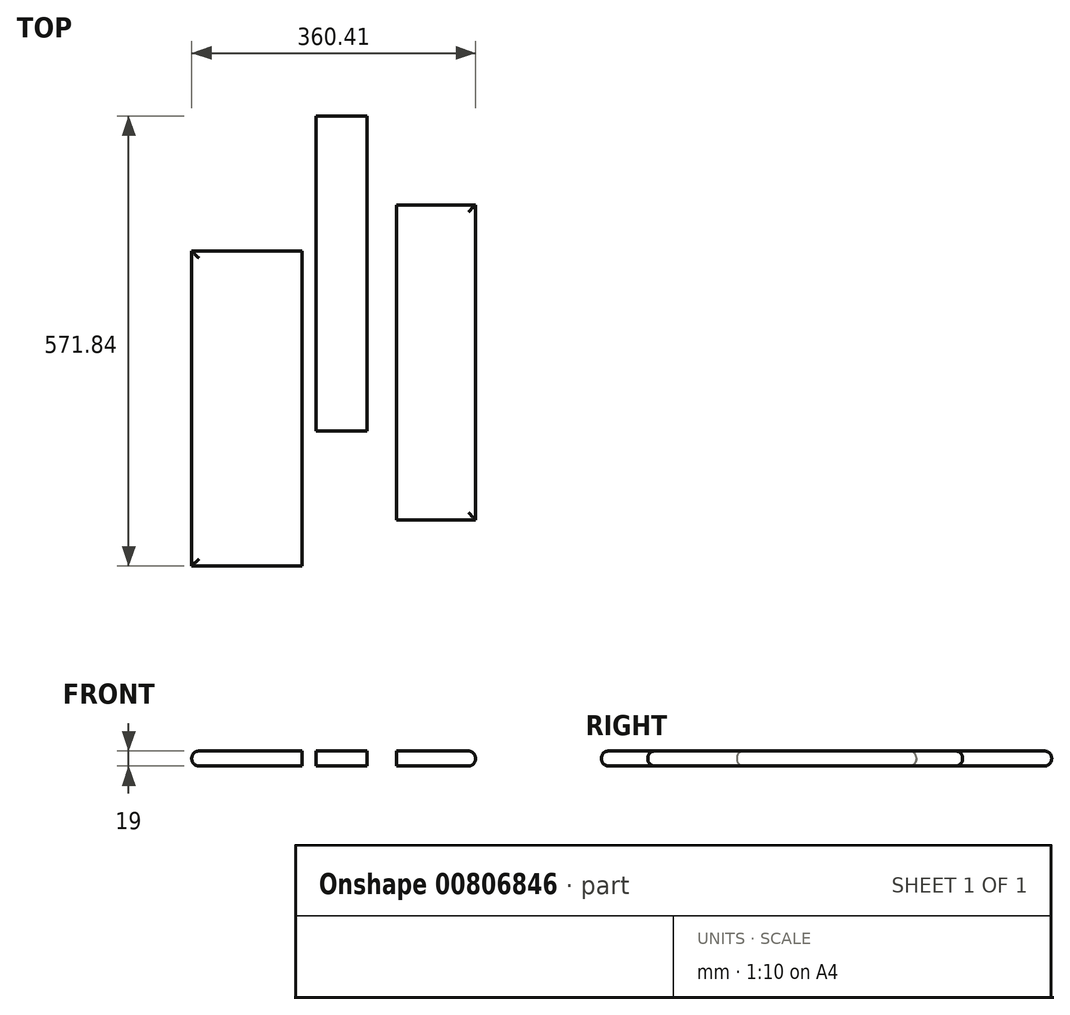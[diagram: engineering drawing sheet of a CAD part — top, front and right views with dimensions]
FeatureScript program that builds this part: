
annotation { "Feature Type Name" : "Feature", "Feature Type Description" : "" }
export const myFeature = defineFeature(function(context is Context, id is Id, definition is map)
    precondition{}
    {
        {
            var Q0;
            Q0=qCreatedBy(makeId("Top.planeOp"),FACE);
            var sketch = newSketch(context, id + "F0", { "sketchPlane" : qUnion([Q0])});
            skLineSegment(sketch, "E0.bottom", {"start": v(-82.9, -190.4) * mm, "end": v(57.1, -190.4) * mm});
            skLineSegment(sketch, "E0.top", {"start": v(-82.9, 209.6) * mm, "end": v(57.1, 209.6) * mm});
            skLineSegment(sketch, "E0.left", {"start": v(-82.9, -190.4) * mm, "end": v(-82.9, 209.6) * mm});
            skLineSegment(sketch, "E0.right", {"start": v(57.1, -190.4) * mm, "end": v(57.1, 209.6) * mm});
            skSolve(sketch);
        }
        {
            var Q0;
            Q0=qCreatedBy(makeId("Top.planeOp"),FACE);
            var sketch = newSketch(context, id + "F1", { "sketchPlane" : qUnion([Q0])});
            skLineSegment(sketch, "E1.bottom", {"start": v(74.78, 381.44) * mm, "end": v(139.78, 381.44) * mm});
            skLineSegment(sketch, "E1.top", {"start": v(74.78, -18.56) * mm, "end": v(139.78, -18.56) * mm});
            skLineSegment(sketch, "E1.left", {"start": v(74.78, 381.44) * mm, "end": v(74.78, -18.56) * mm});
            skLineSegment(sketch, "E1.right", {"start": v(139.78, 381.44) * mm, "end": v(139.78, -18.56) * mm});
            skSolve(sketch);
        }
        {
            var Q0;
            Q0=qCreatedBy(makeId("Top.planeOp"),FACE);
            var sketch = newSketch(context, id + "F2", { "sketchPlane" : qUnion([Q0])});
            skLineSegment(sketch, "E2.bottom", {"start": v(177.5, 268.41) * mm, "end": v(277.5, 268.41) * mm});
            skLineSegment(sketch, "E2.top", {"start": v(177.5, -131.59) * mm, "end": v(277.5, -131.59) * mm});
            skLineSegment(sketch, "E2.left", {"start": v(177.5, 268.41) * mm, "end": v(177.5, -131.59) * mm});
            skLineSegment(sketch, "E2.right", {"start": v(277.5, 268.41) * mm, "end": v(277.5, -131.59) * mm});
            skSolve(sketch);
        }
        {
            var Q0;
            Q0=makeQuery(id+"F0.imprint","IMPRINT",FACE,{"disambiguationData":[TD([[makeQuery(id+"F0.imprint","IMPRINT",EDGE,{"derivedFrom":sQuery(id+"F0.wireOp",EDGE,"E0.bottom")}),1.0]])]});
            extrude(context, id + "F3", {"entities" : qUnion([Q0]), "depth" : 19 * mm, "offsetDistance" : 25 * mm});
        }
        {
            var Q0;
            Q0=makeQuery(id+"F1.imprint","IMPRINT",FACE,{"disambiguationData":[TD([[makeQuery(id+"F1.imprint","IMPRINT",EDGE,{"derivedFrom":sQuery(id+"F1.wireOp",EDGE,"E1.bottom")}),-1.0]])]});
            extrude(context, id + "F4", {"entities" : qUnion([Q0]), "depth" : 19 * mm, "offsetDistance" : 25 * mm});
        }
        {
            var Q0;
            Q0=makeQuery(id+"F2.imprint","IMPRINT",FACE,{"disambiguationData":[TD([[makeQuery(id+"F2.imprint","IMPRINT",EDGE,{"derivedFrom":sQuery(id+"F2.wireOp",EDGE,"E2.bottom")}),-1.0]])]});
            extrude(context, id + "F5", {"entities" : qUnion([Q0]), "depth" : 19 * mm, "offsetDistance" : 25 * mm});
        }
        {
            var Q0;
            Q0=makeQuery(id+"F3.opExtrude","CAP_EDGE",EDGE,{"disambiguationData":[OSD([sQuery(id+"F0.wireOp",EDGE,"E0.bottom")])],"isStart":false});
            var Q1;
            Q1=makeQuery(id+"F3.opExtrude","CAP_EDGE",EDGE,{"disambiguationData":[OSD([sQuery(id+"F0.wireOp",EDGE,"E0.left")])],"isStart":false});
            var Q2;
            Q2=makeQuery(id+"F3.opExtrude","CAP_EDGE",EDGE,{"disambiguationData":[OSD([sQuery(id+"F0.wireOp",EDGE,"E0.top")])],"isStart":false});
            var Q3;
            Q3=makeQuery(id+"F3.opExtrude","CAP_EDGE",EDGE,{"disambiguationData":[OSD([sQuery(id+"F0.wireOp",EDGE,"E0.bottom")])],"isStart":true});
            var Q4;
            Q4=makeQuery(id+"F3.opExtrude","CAP_EDGE",EDGE,{"disambiguationData":[OSD([sQuery(id+"F0.wireOp",EDGE,"E0.left")])],"isStart":true});
            var Q5;
            Q5=makeQuery(id+"F3.opExtrude","CAP_EDGE",EDGE,{"disambiguationData":[OSD([sQuery(id+"F0.wireOp",EDGE,"E0.top")])],"isStart":true});
            fillet(context, id + "F6", {"entities" : qUnion([Q0, Q1, Q2, Q3, Q4, Q5]), "radius" : 9 * mm, "tangentPropagation" : true, "allowEdgeOverflow" : false});
        }
        {
            var Q0;
            Q0=makeQuery(id+"F4.opExtrude","CAP_EDGE",EDGE,{"disambiguationData":[OSD([sQuery(id+"F1.wireOp",EDGE,"E1.bottom")])],"isStart":false});
            var Q1;
            Q1=makeQuery(id+"F4.opExtrude","CAP_EDGE",EDGE,{"disambiguationData":[OSD([sQuery(id+"F1.wireOp",EDGE,"E1.bottom")])],"isStart":true});
            var Q2;
            Q2=makeQuery(id+"F4.opExtrude","CAP_EDGE",EDGE,{"disambiguationData":[OSD([sQuery(id+"F1.wireOp",EDGE,"E1.top")])],"isStart":false});
            var Q3;
            Q3=makeQuery(id+"F4.opExtrude","CAP_EDGE",EDGE,{"disambiguationData":[OSD([sQuery(id+"F1.wireOp",EDGE,"E1.top")])],"isStart":true});
            fillet(context, id + "F7", {"entities" : qUnion([Q0, Q1, Q2, Q3]), "radius" : 9 * mm, "tangentPropagation" : true, "allowEdgeOverflow" : false});
        }
        {
            var Q0;
            Q0=makeQuery(id+"F5.opExtrude","CAP_EDGE",EDGE,{"disambiguationData":[OSD([sQuery(id+"F2.wireOp",EDGE,"E2.top")])],"isStart":false});
            var Q1;
            Q1=makeQuery(id+"F5.opExtrude","CAP_EDGE",EDGE,{"disambiguationData":[OSD([sQuery(id+"F2.wireOp",EDGE,"E2.top")])],"isStart":true});
            var Q2;
            Q2=makeQuery(id+"F5.opExtrude","CAP_EDGE",EDGE,{"disambiguationData":[OSD([sQuery(id+"F2.wireOp",EDGE,"E2.right")])],"isStart":false});
            var Q3;
            Q3=makeQuery(id+"F5.opExtrude","CAP_EDGE",EDGE,{"disambiguationData":[OSD([sQuery(id+"F2.wireOp",EDGE,"E2.right")])],"isStart":true});
            var Q4;
            Q4=makeQuery(id+"F5.opExtrude","CAP_EDGE",EDGE,{"disambiguationData":[OSD([sQuery(id+"F2.wireOp",EDGE,"E2.bottom")])],"isStart":false});
            var Q5;
            Q5=makeQuery(id+"F5.opExtrude","CAP_EDGE",EDGE,{"disambiguationData":[OSD([sQuery(id+"F2.wireOp",EDGE,"E2.bottom")])],"isStart":true});
            fillet(context, id + "F8", {"entities" : qUnion([Q0, Q1, Q2, Q3, Q4, Q5]), "radius" : 9 * mm, "tangentPropagation" : true, "allowEdgeOverflow" : false});
        }
    });
